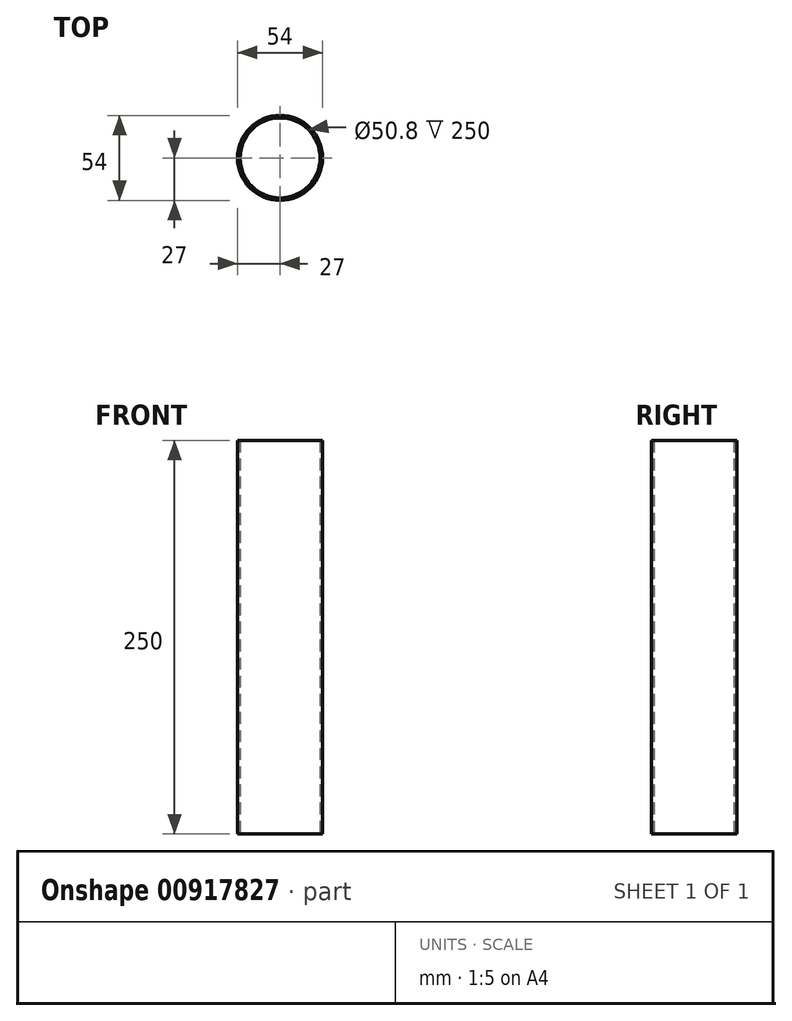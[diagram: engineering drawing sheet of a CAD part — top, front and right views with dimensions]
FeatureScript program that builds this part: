
annotation { "Feature Type Name" : "Feature", "Feature Type Description" : "" }
export const myFeature = defineFeature(function(context is Context, id is Id, definition is map)
    precondition{}
    {
        {
            var Q0;
            Q0=qCreatedBy(makeId("Top.planeOp"),FACE);
            var sketch = newSketch(context, id + "F0", { "sketchPlane" : qUnion([Q0])});
            skCircle(sketch, "E0", {"center": v(0, 0) * mm, "radius": 25.4 * mm});
            skCircle(sketch, "E1", {"center": v(0, 0) * mm, "radius": 27 * mm});
            skSolve(sketch);
        }
        {
            var Q0;
            Q0=makeQuery(id+"F0.imprint","IMPRINT",FACE,{"disambiguationData":[TD([[makeQuery(id+"F0.imprint","IMPRINT",EDGE,{"derivedFrom":sQuery(id+"F0.wireOp",EDGE,"E0")}),-1.0]])]});
            extrude(context, id + "F1", {"entities" : qUnion([Q0]), "depth" : 250 * mm, "offsetDistance" : 25 * mm});
        }
    });
